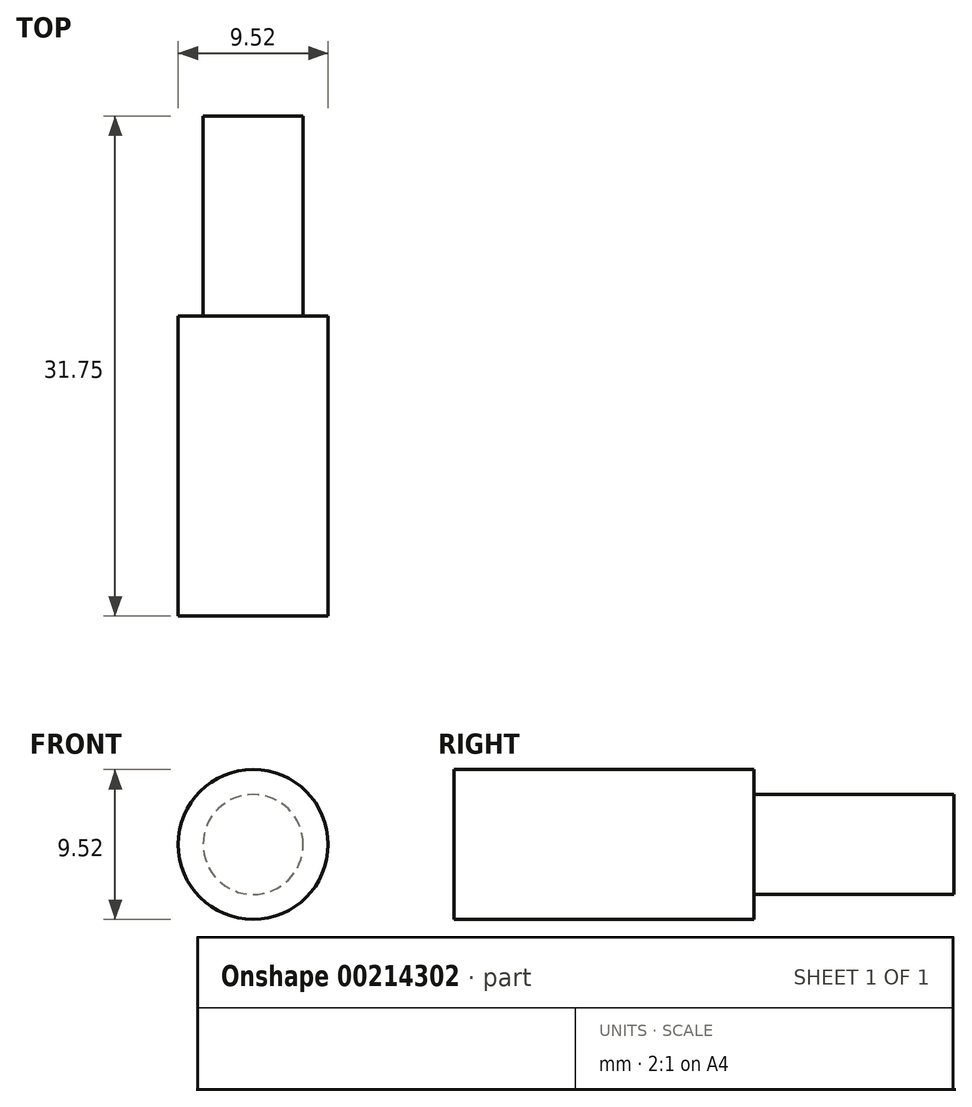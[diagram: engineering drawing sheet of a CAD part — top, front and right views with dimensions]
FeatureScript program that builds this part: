
annotation { "Feature Type Name" : "Feature", "Feature Type Description" : "" }
export const myFeature = defineFeature(function(context is Context, id is Id, definition is map)
    precondition{}
    {
        {
            var Q0;
            Q0=qCreatedBy(makeId("Front.planeOp"),FACE);
            var sketch = newSketch(context, id + "F0", { "sketchPlane" : qUnion([Q0])});
            skCircle(sketch, "E0", {"center": v(0, 0) * mm, "radius": 4.76 * mm});
            skCircle(sketch, "E1", {"center": v(0, 0) * mm, "radius": 3.18 * mm});
            skSolve(sketch);
        }
        {
            var Q0;
            Q0=makeQuery(id+"F0.imprint","IMPRINT",FACE,{"disambiguationData":[TD([[makeQuery(id+"F0.imprint","IMPRINT",EDGE,{"derivedFrom":sQuery(id+"F0.wireOp",EDGE,"E0")}),1.0]])]});
            var Q1;
            Q1=makeQuery(id+"F0.imprint","IMPRINT",FACE,{"disambiguationData":[TD([[makeQuery(id+"F0.imprint","IMPRINT",EDGE,{"derivedFrom":sQuery(id+"F0.wireOp",EDGE,"E1")}),1.0]])]});
            extrude(context, id + "F1", {"entities" : qUnion([Q0, Q1]), "depth" : 19.05 * mm});
        }
        {
            var Q0;
            Q0=makeQuery(id+"F0.imprint","IMPRINT",FACE,{"disambiguationData":[TD([[makeQuery(id+"F0.imprint","IMPRINT",EDGE,{"derivedFrom":sQuery(id+"F0.wireOp",EDGE,"E1")}),1.0]])]});
            extrude(context, id + "F2", {"entities" : qUnion([Q0]), "operationType" : NewBodyOperationType.ADD, "oppositeDirection" : true, "depth" : 12.7 * mm});
        }
    });
